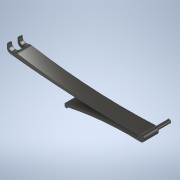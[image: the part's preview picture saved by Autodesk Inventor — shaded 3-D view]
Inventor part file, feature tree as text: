
AUTODESK INVENTOR PART (.ipt)
format: ipt  version: 2021 (Build 250183000, 183)  size: 161,792 bytes
history: native  units: in
note: dims shown in document units (in); Inventor stores cm internally (conversion verified against a paired STEP export)
features: extrude x3, fillet x2, sketch x2, plane x1, projected_geometry x1
ambient origin geometry x8: Origin, YZ Plane, XZ Plane, XY Plane, X Axis, Y Axis, Z Axis, Center Point
bodies: Body1 (feature_tree)
feature tree (9):
  extrude  "Extrusion2"  Depth=0.5906in
  plane  "Work Plane1"
  extrude  "Extrusion3"  Depth=0.0197in
  fillet  "Fillet1"  Radius=0.1575in
  fillet  "Fillet2"  Radius=0.1575in
  extrude  "Extrusion4"  Depth=0.0787in
  sketch  "Sketch1"  dims[d0=1.7717in d1=0.5906in]
  sketch  "Sketch3"  dims[d4=0.0236in d6=0.0295in d9=0.1575in d10=0.0in d11=0.1575in d12=0.0in d13=0.0787in d14=0.0394in d15=0.0394in d16=0.1575in d17=0.0in d19=0.0394in d20=0.0394in d22=0.0197in]
  projected_geometry  "Projected Loop1"
